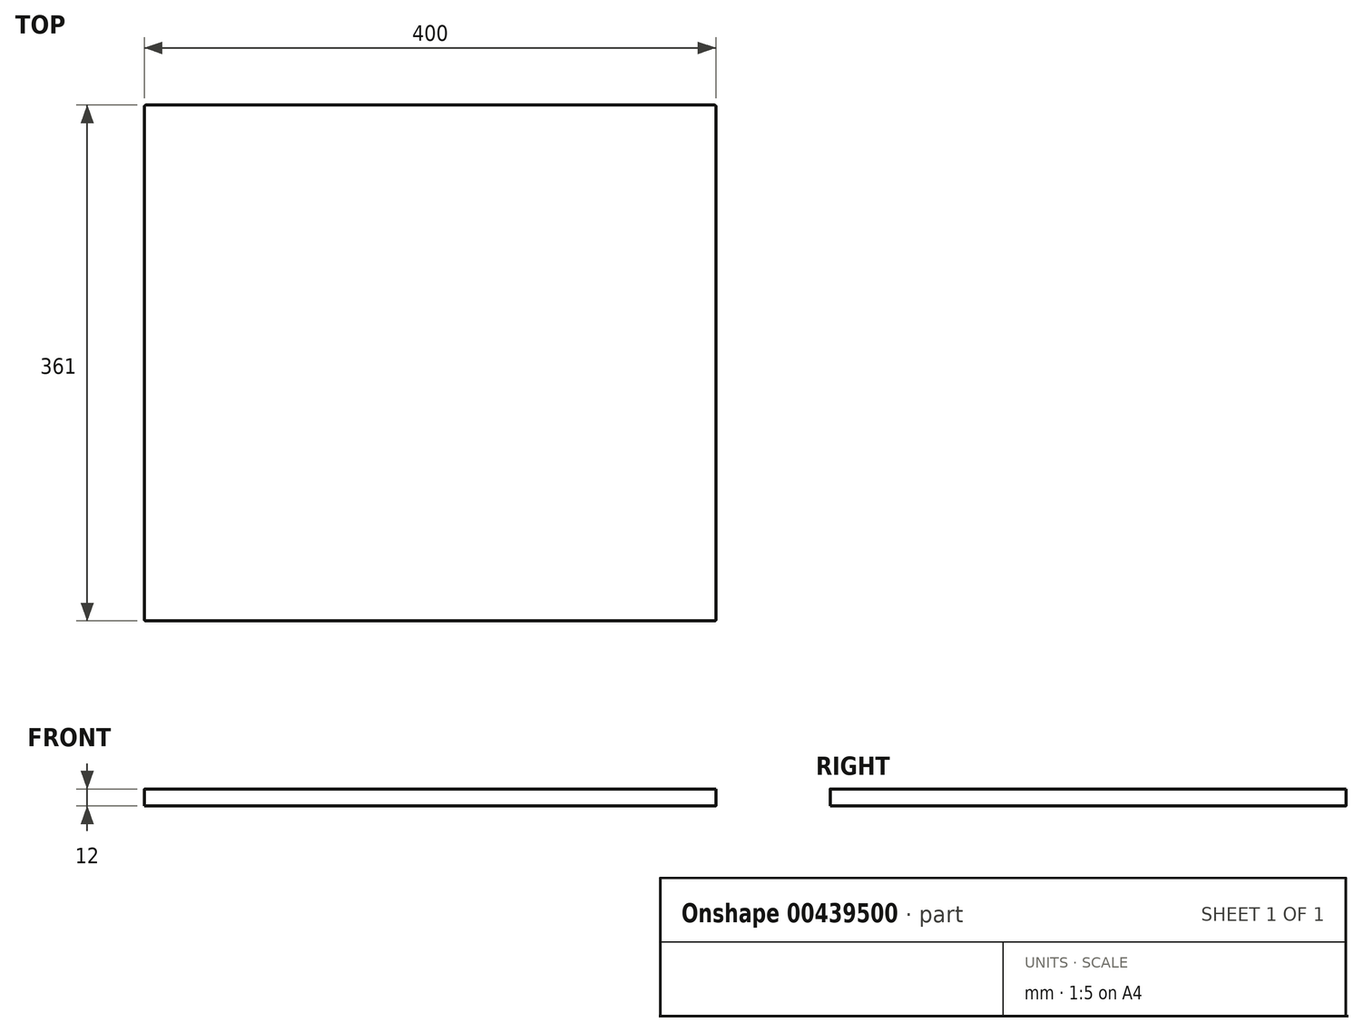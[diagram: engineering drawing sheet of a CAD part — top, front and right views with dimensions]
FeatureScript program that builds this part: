
annotation { "Feature Type Name" : "Feature", "Feature Type Description" : "" }
export const myFeature = defineFeature(function(context is Context, id is Id, definition is map)
    precondition{}
    {
        {
            var Q0;
            Q0=qCreatedBy(makeId("Right.planeOp"),FACE);
            var sketch = newSketch(context, id + "F0", { "sketchPlane" : qUnion([Q0])});
            skLineSegment(sketch, "E0.bottom", {"start": v(0, 0) * mm, "end": v(361, 0) * mm});
            skLineSegment(sketch, "E0.top", {"start": v(0, 12) * mm, "end": v(361, 12) * mm});
            skLineSegment(sketch, "E0.left", {"start": v(0, 0) * mm, "end": v(0, 12) * mm});
            skLineSegment(sketch, "E0.right", {"start": v(361, 0) * mm, "end": v(361, 12) * mm});
            skSolve(sketch);
        }
        {
            var Q0;
            Q0=makeQuery(id+"F0.imprint","IMPRINT",FACE,{"disambiguationData":[TD([[makeQuery(id+"F0.imprint","IMPRINT",EDGE,{"derivedFrom":sQuery(id+"F0.wireOp",EDGE,"E0.bottom")}),1.0]])]});
            extrude(context, id + "F1", {"entities" : qUnion([Q0]), "depth" : 400 * mm, "offsetDistance" : 25 * mm, "symmetric" : true});
        }
        {
            var Q0;
            Q0=makeQuery(id+"F1.opExtrude","CAP_EDGE",EDGE,{"disambiguationData":[OSD([sQuery(id+"F0.wireOp",EDGE,"E0.left")])],"isStart":true});
            var Q1;
            Q1=makeQuery(id+"F1.opExtrude","CAP_EDGE",EDGE,{"disambiguationData":[OSD([sQuery(id+"F0.wireOp",EDGE,"E0.left")])],"isStart":false});
            var Q2;
            Q2=makeQuery(id+"F1.opExtrude","CAP_EDGE",EDGE,{"disambiguationData":[OSD([sQuery(id+"F0.wireOp",EDGE,"E0.right")])],"isStart":false});
            var Q3;
            Q3=makeQuery(id+"F1.opExtrude","CAP_EDGE",EDGE,{"disambiguationData":[OSD([sQuery(id+"F0.wireOp",EDGE,"E0.right")])],"isStart":true});
            fillet(context, id + "F2", {"entities" : qUnion([Q0, Q1, Q2, Q3]), "radius" : 1 * mm, "tangentPropagation" : true, "allowEdgeOverflow" : false});
        }
    });
